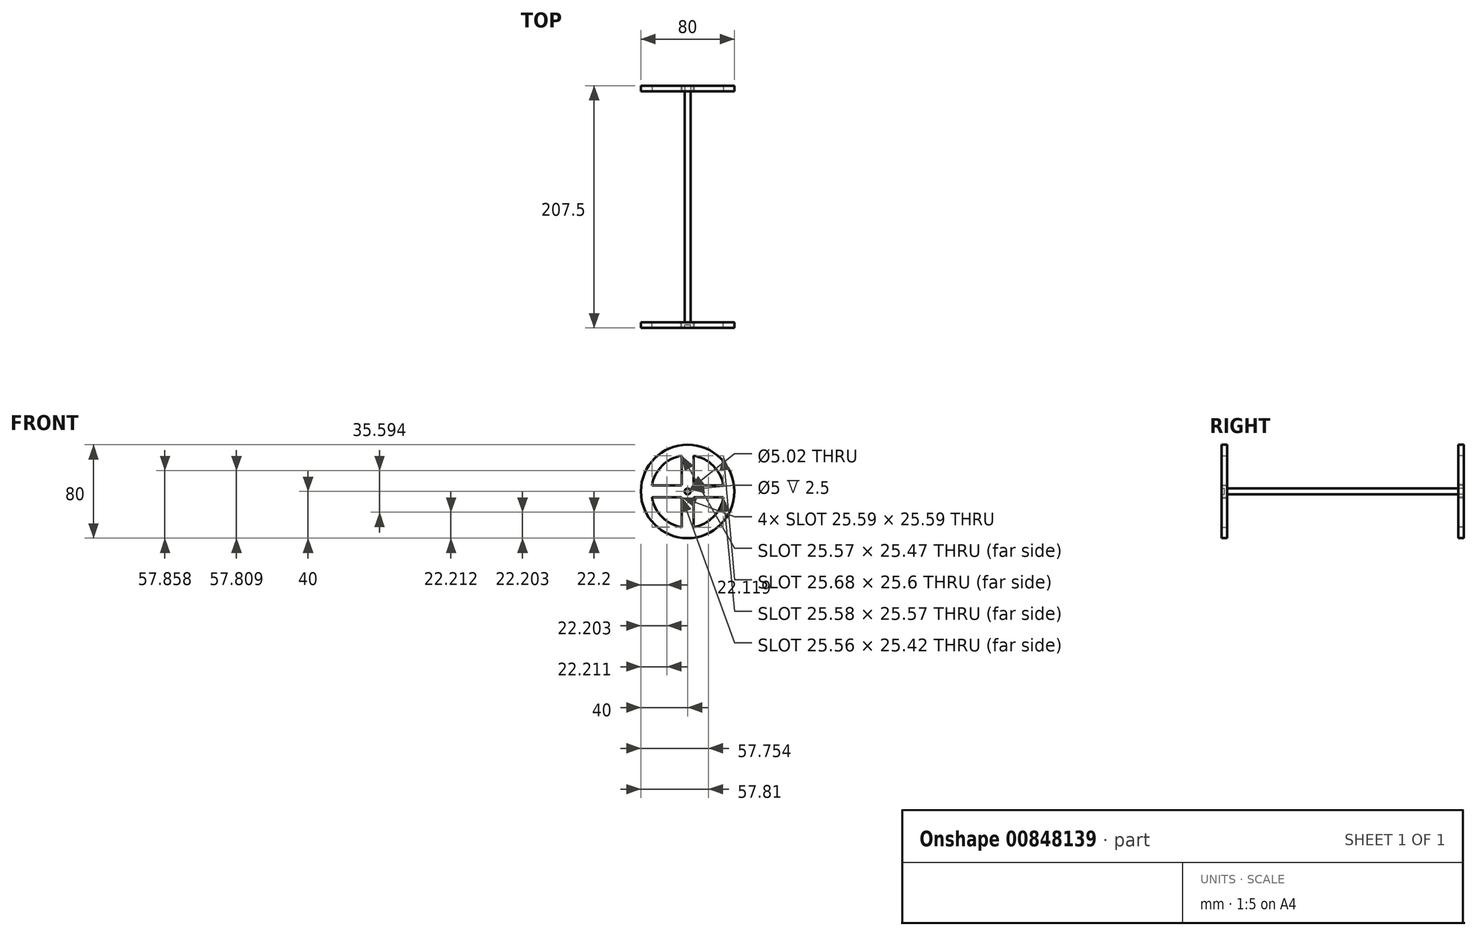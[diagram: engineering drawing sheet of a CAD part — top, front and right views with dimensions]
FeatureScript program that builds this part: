
annotation { "Feature Type Name" : "Feature", "Feature Type Description" : "" }
export const myFeature = defineFeature(function(context is Context, id is Id, definition is map)
    precondition{}
    {
        {
            var Q0;
            Q0=qCreatedBy(makeId("Front.planeOp"),FACE);
            var sketch = newSketch(context, id + "F0", { "sketchPlane" : qUnion([Q0])});
            skCircle(sketch, "E0", {"center": v(0, 0) * mm, "radius": 40 * mm});
            skPoint(sketch, "E0.first.point", {"position": v(-29.47, 27.05) * mm});
            skPoint(sketch, "E0.second.point", {"position": v(30.51, -25.87) * mm});
            skPoint(sketch, "E0.third.point", {"position": v(18.2, -35.62) * mm});
            skArc(sketch, "E1", {"start": v(-5, 30.6) * mm, "mid": v(-21.92, 21.92) * mm, "end": v(-30.6, 5) * mm});
            skPoint(sketch, "E1.first.point", {"position": v(-25.57, 17.53) * mm});
            skPoint(sketch, "E1.second.point", {"position": v(26.84, -15.5) * mm});
            skPoint(sketch, "E1.third.point", {"position": v(0, -31) * mm});
            skArc(sketch, "E2", {"start": v(-5.6, -5) * mm, "mid": v(-5.3, -5.3) * mm, "end": v(-5, -5.6) * mm});
            skPoint(sketch, "E2.first.point", {"position": v(6.94, -2.85) * mm});
            skPoint(sketch, "E2.second.point", {"position": v(-1.98, 7.23) * mm});
            skPoint(sketch, "E2.third.point", {"position": v(0, 7.5) * mm});
            skCircle(sketch, "E3", {"center": v(0, 0) * mm, "radius": 2.5 * mm});
            skPoint(sketch, "E3.first.point", {"position": v(1.32, -2.12) * mm});
            skPoint(sketch, "E3.second.point", {"position": v(-1.53, 1.98) * mm});
            skPoint(sketch, "E3.third.point", {"position": v(0, 2.5) * mm});
            skLineSegment(sketch, "E4", {"start": v(0, 0) * mm, "end": v(0, 31) * mm});
            skLineSegment(sketch, "E5", {"start": v(0, 31) * mm, "end": v(0, -31) * mm, "construction": true});
            skLineSegment(sketch, "E6", {"start": v(-31, 0) * mm, "end": v(31, 0) * mm, "construction": true});
            skLineSegment(sketch, "E7.0", {"start": v(-5, 30.6) * mm, "end": v(-5, 5.6) * mm});
            skLineSegment(sketch, "E8.0", {"start": v(-30.6, -5) * mm, "end": v(-5.6, -5) * mm});
            skLineSegment(sketch, "E9.trimOffspring", {"start": v(5, 30.6) * mm, "end": v(5, 5.6) * mm});
            skLineSegment(sketch, "E10.trimOffspring", {"start": v(-30.6, 5) * mm, "end": v(-5.6, 5) * mm});
            skPoint(sketch, "E11.orphan", {"position": v(-40, 0) * mm});
            skArc(sketch, "E12.trimOffspring", {"start": v(30.6, 5) * mm, "mid": v(21.92, 21.92) * mm, "end": v(5, 30.6) * mm});
            skArc(sketch, "E13.trimOffspring", {"start": v(5, -30.6) * mm, "mid": v(21.92, -21.92) * mm, "end": v(30.6, -5) * mm});
            skArc(sketch, "E14.trimOffspring", {"start": v(-30.6, -5) * mm, "mid": v(-21.92, -21.92) * mm, "end": v(-5, -30.6) * mm});
            skArc(sketch, "E15.trimOffspring", {"start": v(5, -5.6) * mm, "mid": v(5.3, -5.3) * mm, "end": v(5.6, -5) * mm});
            skArc(sketch, "E16.trimOffspring", {"start": v(5.6, 5) * mm, "mid": v(5.3, 5.3) * mm, "end": v(5, 5.6) * mm});
            skArc(sketch, "E17.trimOffspring", {"start": v(-5, 5.6) * mm, "mid": v(-5.3, 5.3) * mm, "end": v(-5.6, 5) * mm});
            skLineSegment(sketch, "E18.trimOffspring", {"start": v(5.6, -5) * mm, "end": v(30.6, -5) * mm});
            skLineSegment(sketch, "E19.trimOffspring", {"start": v(-5, -5.6) * mm, "end": v(-5, -30.6) * mm});
            skLineSegment(sketch, "E20.trimOffspring", {"start": v(5, -5.6) * mm, "end": v(5, -30.6) * mm});
            skLineSegment(sketch, "E21.trimOffspring", {"start": v(5.6, 5) * mm, "end": v(30.6, 5) * mm});
            skSolve(sketch);
        }
        {
            var Q0;
            Q0=makeQuery(id+"F0.imprint","IMPRINT",FACE,{"disambiguationData":[TD([[makeQuery(id+"F0.imprint","IMPRINT",EDGE,{"derivedFrom":sQuery(id+"F0.wireOp",EDGE,"E0")}),1.0]])]});
            extrude(context, id + "F1", {"entities" : qUnion([Q0]), "endBound" : BoundingType.SYMMETRIC, "depth" : 5 * mm, "offsetDistance" : 25 * mm});
        }
        {
            var Q0;
            Q0=qCreatedBy(makeId("Front.planeOp"),FACE);
            var sketch = newSketch(context, id + "F2", { "sketchPlane" : qUnion([Q0])});
            skCircle(sketch, "E22", {"center": v(0, 0) * mm, "radius": 2.5 * mm});
            skPoint(sketch, "E22.first.point", {"position": v(2.01, -1.49) * mm});
            skPoint(sketch, "E22.second.point", {"position": v(-2.04, 1.44) * mm});
            skPoint(sketch, "E22.third.point", {"position": v(-2.5, 0) * mm});
            skSolve(sketch);
        }
        {
            var Q0;
            Q0=makeQuery(id+"F2.imprint","IMPRINT",FACE,{"disambiguationData":[TD([[makeQuery(id+"F2.imprint","IMPRINT",EDGE,{"derivedFrom":sQuery(id+"F2.wireOp",EDGE,"E22")}),1.0]])]});
            extrude(context, id + "F3", {"entities" : qUnion([Q0]), "operationType" : NewBodyOperationType.ADD, "oppositeDirection" : true, "depth" : 200 * mm, "offsetDistance" : 25 * mm});
        }
        {
            var Q0;
            Q0=makeQuery(id+"F3.opExtrude","CAP_FACE",FACE,{"disambiguationData":[OSD([sQuery(id+"F2.wireOp",EDGE,"E22")])],"isStart":false});
            var sketch = newSketch(context, id + "F4", { "sketchPlane" : qUnion([Q0])});
            skCircle(sketch, "E23", {"center": v(0, 0) * mm, "radius": 40 * mm});
            skCircle(sketch, "E24", {"center": v(0, 0) * mm, "radius": 2.5 * mm});
            skArc(sketch, "E25", {"start": v(5.17, -5.43) * mm, "mid": v(5.38, -5.23) * mm, "end": v(5.58, -5.01) * mm});
            skArc(sketch, "E26", {"start": v(30.57, 5.12) * mm, "mid": v(21.88, 21.96) * mm, "end": v(5, 30.6) * mm});
            skLineSegment(sketch, "E27", {"start": v(-5.58, 5.01) * mm, "end": v(-30.6, 5.01) * mm});
            skLineSegment(sketch, "E28", {"start": v(-30.6, -5.01) * mm, "end": v(-5.58, -5.01) * mm});
            skLineSegment(sketch, "E29", {"start": v(-5.03, -30.59) * mm, "end": v(-5.03, -5.57) * mm});
            skLineSegment(sketch, "E30", {"start": v(5.17, -30.57) * mm, "end": v(5.17, -5.43) * mm});
            skLineSegment(sketch, "E31", {"start": v(30.6, -5.01) * mm, "end": v(5.58, -5.01) * mm});
            skLineSegment(sketch, "E32", {"start": v(5.48, 5.12) * mm, "end": v(30.57, 5.12) * mm});
            skLineSegment(sketch, "E33", {"start": v(5, 5.59) * mm, "end": v(5, 30.6) * mm});
            skLineSegment(sketch, "E34", {"start": v(-4.92, 5.66) * mm, "end": v(-4.92, 30.6) * mm});
            skCircle(sketch, "E35", {"center": v(0, 0) * mm, "radius": 2.51 * mm});
            skArc(sketch, "E36.trimOffspring", {"start": v(5.48, 5.12) * mm, "mid": v(5.25, 5.36) * mm, "end": v(5, 5.59) * mm});
            skArc(sketch, "E37.trimOffspring", {"start": v(-4.92, 5.66) * mm, "mid": v(-5.26, 5.35) * mm, "end": v(-5.58, 5.01) * mm});
            skArc(sketch, "E38.trimOffspring", {"start": v(-5.58, -5.01) * mm, "mid": v(-5.31, -5.3) * mm, "end": v(-5.03, -5.57) * mm});
            skArc(sketch, "E39.trimOffspring", {"start": v(5.17, -30.57) * mm, "mid": v(21.98, -21.86) * mm, "end": v(30.6, -5.01) * mm});
            skArc(sketch, "E40.trimOffspring", {"start": v(-30.6, -5.01) * mm, "mid": v(-21.93, -21.91) * mm, "end": v(-5.03, -30.59) * mm});
            skArc(sketch, "E41.trimOffspring", {"start": v(-4.92, 30.6) * mm, "mid": v(-21.89, 21.95) * mm, "end": v(-30.6, 5.01) * mm});
            skSolve(sketch);
        }
        {
            var Q0;
            Q0=makeQuery(id+"F4.imprint","IMPRINT",FACE,{"disambiguationData":[TD([[makeQuery(id+"F4.imprint","IMPRINT",EDGE,{"derivedFrom":sQuery(id+"F4.wireOp",EDGE,"E23")}),1.0]])]});
            extrude(context, id + "F5", {"entities" : qUnion([Q0]), "depth" : 5 * mm, "offsetDistance" : 25 * mm});
        }
    });
